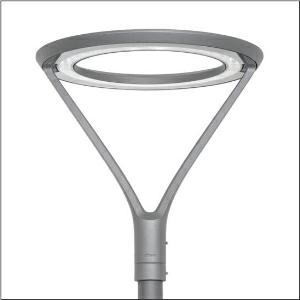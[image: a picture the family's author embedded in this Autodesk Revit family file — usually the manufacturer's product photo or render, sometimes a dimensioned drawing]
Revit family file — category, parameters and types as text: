
# Revit family: dl_r__20___st1_2a_5xa51283wa008p_0b9f
name_source: partatom
category: Lighting Fixtures
units: mm (PartAtom-declared; Revit-internal decimal feet)

## family parameters
Cut with Voids When Loaded = No
Host = Face
Light Source = No
Part Type = Normal
Room Calculation Point = No
Round Connector Dimension = Use Diameter
Shared = No

## types (1)
- --- (1 x LED, 4200 lm, 34.3 W, 3000K)
    Apparent Load = 34 VA
    CIE Flux Codes = 32 72 97 100 100
    Color Rendering = 70
    Color Temperature = 3000K
    Default Elevation = 1800 mm
    Description = DL® 20, mast luminaire, primary light control with reflector, highly specular, primary optical cover: cover, of toughened safety glass of clear glass with excellent transmission level, light distribution: ST1.2a, light emission: direct distribution, primary light characteristic: asymmetric, installation type: post-top, LED, High Power LED, rated luminous flux: 4.180lm, luminous efficacy: 79lm/W, light colour: 730, colour temperature: 3000K, control gear: ECG Plus, control: overheat protection, power reduction, digital communication interface, constant luminous flux control, time-dependent luminous flux control, flexible luminous flux parameterisation, electronic power reduction, mains connection: 230..240V, 50/60Hz, connection cable pre-assembled, cable length: 5m, start of lifetime: 53W, end of service life: 54W, reduction: 24W, luminaire housing, upper part, of cast aluminium, powder-coated, Siteco® metallic grey (DB 702S), diameter: 690mm, height: 690mm, spigot size: 76mm (post-top), luminaire housing, of cast aluminium, powder-coated, Siteco® metallic grey (DB 702S), equipment: Power, protection rating (complete): IP66, insulation class (complete): insulation class II (safety insulation), certification: CE, ENEC, VDE, impact resistance: IK08, permissible operating ambient temperature: -25..+30°C, standard-compliant lighting for roads and squares, packaging unit: 1 piece

Light Distribution: ST1.2a
    Height = 690 mm
    Lamp = 1 x LED
    Lamp Light Flux = 4200 lm
    Lamp Power = 34.3 W
    Lamp count = 1
    Length = 690 mm
    Luminous efficacy = 122 lm/W
    Manufacturer = Siteco
    ModVariant = No
    Model = 5XA51283WA008P
    Number of Poles = 1
    OnlyDefault = Yes
    Power Factor = 1
    Product Name = DL® 20 | ST1.2a
    Product group = mast luminaire | pylon top
    ProductGroupID = 6100
    Protection Class = Protection class II
    Protection Degree = IP 66
    RLX_Detail_Level = 1
    RLX_Emergency_Light_Flux = 0 lm
    RLX_Emergency_Type = 0
    RLX_Emergency_Type_DB = No
    RlxData = <blob elided: 207009 chars, md5=6386286e>
    Socket = socket
    Standby Power = 0 W
    System Light Flux = 4200 lm
    System Power = 34 W
    Type Comments = factory setting: luminous flux: 100 % | dim-lin: 254 | 464 mA
    Type Image = l_1006001.jpg
    URL = http://relux.com
    VarID = @adj_009523
    Voltage = 0 V
    Weight = 0.00 kg
    Width = 0 mm  [stored 0 ft]

note: [stored X ft] marks values corroborated as IEEE doubles in the binary element streams (Revit-internal decimal feet)

## geometry (parser evidence)
native form markers: Blend x4, Sweep x11
no freeform markers — native parametric forms only
